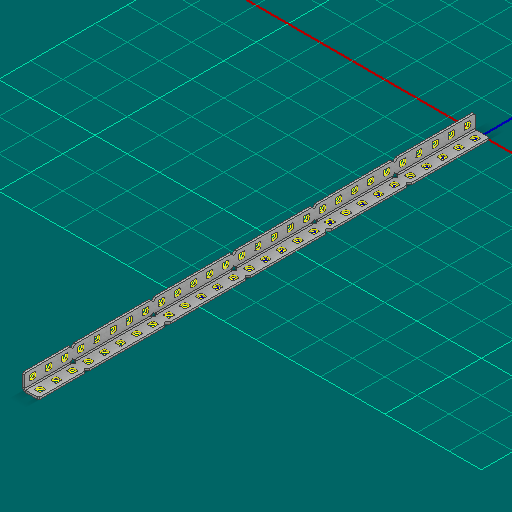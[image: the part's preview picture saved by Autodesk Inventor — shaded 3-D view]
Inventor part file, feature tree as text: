
AUTODESK INVENTOR PART (.ipt)
format: ipt  version: 2025 (Build 290162000, 162)  size: 1,141,760 bytes
history: native  units: in
note: dims shown in document units (in); Inventor stores cm internally (conversion verified against a paired STEP export)
features: other x121, sketch x2, sheet_metal_op x1
ambient origin geometry x8: Origin, YZ Plane, XZ Plane, XY Plane, X Axis, Y Axis, Z Axis, Center Point
bodies: Solid1 (feature_tree)
feature tree (124):
  other  "Alu Angle 1x1x28.ipt"
  other  "Solid1::Alu Angle 1x1x28.ipt"
  other  "TaggingFeature1"
  sketch  "Sketch1"  dims[d0=0.3937in]
  sketch  "Sketch2"  dims[d1=0.0625in]
  sheet_metal_op  "Body Pattern Sketch"
  other  "Arc Length"
  other  "Diagonal Plane"
  other  "Srf1"
  other  "Srf2"
  other  "Srf3"
  other  "Srf4"
  other  "Srf5"
  other  "Srf6"
  other  "Srf7"
  other  "Srf8"
  other  "Srf9"
  other  "Srf10"
  other  "Srf11"
  other  "Srf12"
  other  "Srf13"
  other  "Srf14"
  other  "Srf15"
  other  "Srf16"
  other  "Srf17"
  other  "Srf18"
  other  "Srf19"
  other  "Srf20"
  other  "Srf21"
  other  "Srf22"
  other  "Srf23"
  other  "Srf24"
  other  "Srf25"
  other  "Srf26"
  other  "Srf27"
  other  "Srf28"
  other  "Srf29"
  other  "Srf30"
  other  "Srf31"
  other  "Srf32"
  other  "Srf33"
  other  "Srf34"
  other  "Srf35"
  other  "Srf36"
  other  "Srf37"
  other  "Srf38"
  other  "Srf39"
  other  "Srf40"
  other  "Srf41"
  other  "Srf42"
  other  "Srf43"
  other  "Srf44"
  other  "Srf45"
  other  "Srf46"
  other  "Srf47"
  other  "Srf48"
  other  "Srf49"
  other  "Srf50"
  other  "Srf51"
  other  "Srf52"
  other  "Srf53"
  other  "Srf54"
  other  "Srf55"
  other  "Srf56"
  other  "Srf57"
  other  "Srf58"
  other  "Srf91::Derived"
  other  "Srf92::Derived"
  other  "Srf856::Derived"
  other  "Srf857::Derived"
  other  "Srf858::Derived"
  other  "Srf859::Derived"
  other  "Srf860::Derived"
  other  "Srf861::Derived"
  other  "Srf1383::Derived"
  other  "Srf1384::Derived"
  other  "Srf1385::Derived"
  other  "Srf1386::Derived"
  other  "Srf1387::Derived"
  other  "Srf1388::Derived"
  other  "Srf1389::Derived"
  other  "Srf1390::Derived"
  other  "Srf1391::Derived"
  other  "Srf1392::Derived"
  other  "Srf1393::Derived"
  other  "Srf1394::Derived"
  other  "Srf1395::Derived"
  other  "Srf1396::Derived"
  other  "Srf1397::Derived"
  other  "Srf1398::Derived"
  other  "Srf1399::Derived"
  other  "Srf1400::Derived"
  other  "Srf1401::Derived"
  other  "Srf1402::Derived"
  other  "Srf1403::Derived"
  other  "Srf1275::Derived"
  other  "Srf1276::Derived"
  other  "Srf1278::Derived"
  other  "Srf1279::Derived"
  other  "Srf1280::Derived"
  other  "Srf1281::Derived"
  other  "Srf1282::Derived"
  other  "Srf1283::Derived"
  other  "Srf1475::Derived"
  other  "Srf1476::Derived"
  other  "Srf1477::Derived"
  other  "Srf1478::Derived"
  other  "Srf1479::Derived"
  other  "Srf1480::Derived"
  other  "Srf1481::Derived"
  other  "Srf1482::Derived"
  other  "Srf1483::Derived"
  other  "Srf1484::Derived"
  other  "Srf1485::Derived"
  other  "Srf1486::Derived"
  other  "Srf1487::Derived"
  other  "Srf1488::Derived"
  other  "Srf1489::Derived"
  other  "Srf1490::Derived"
  other  "Srf1491::Derived"
  other  "Srf1492::Derived"
  other  "Srf1493::Derived"
  other  "Srf1494::Derived"
  other  "Srf1495::Derived"
